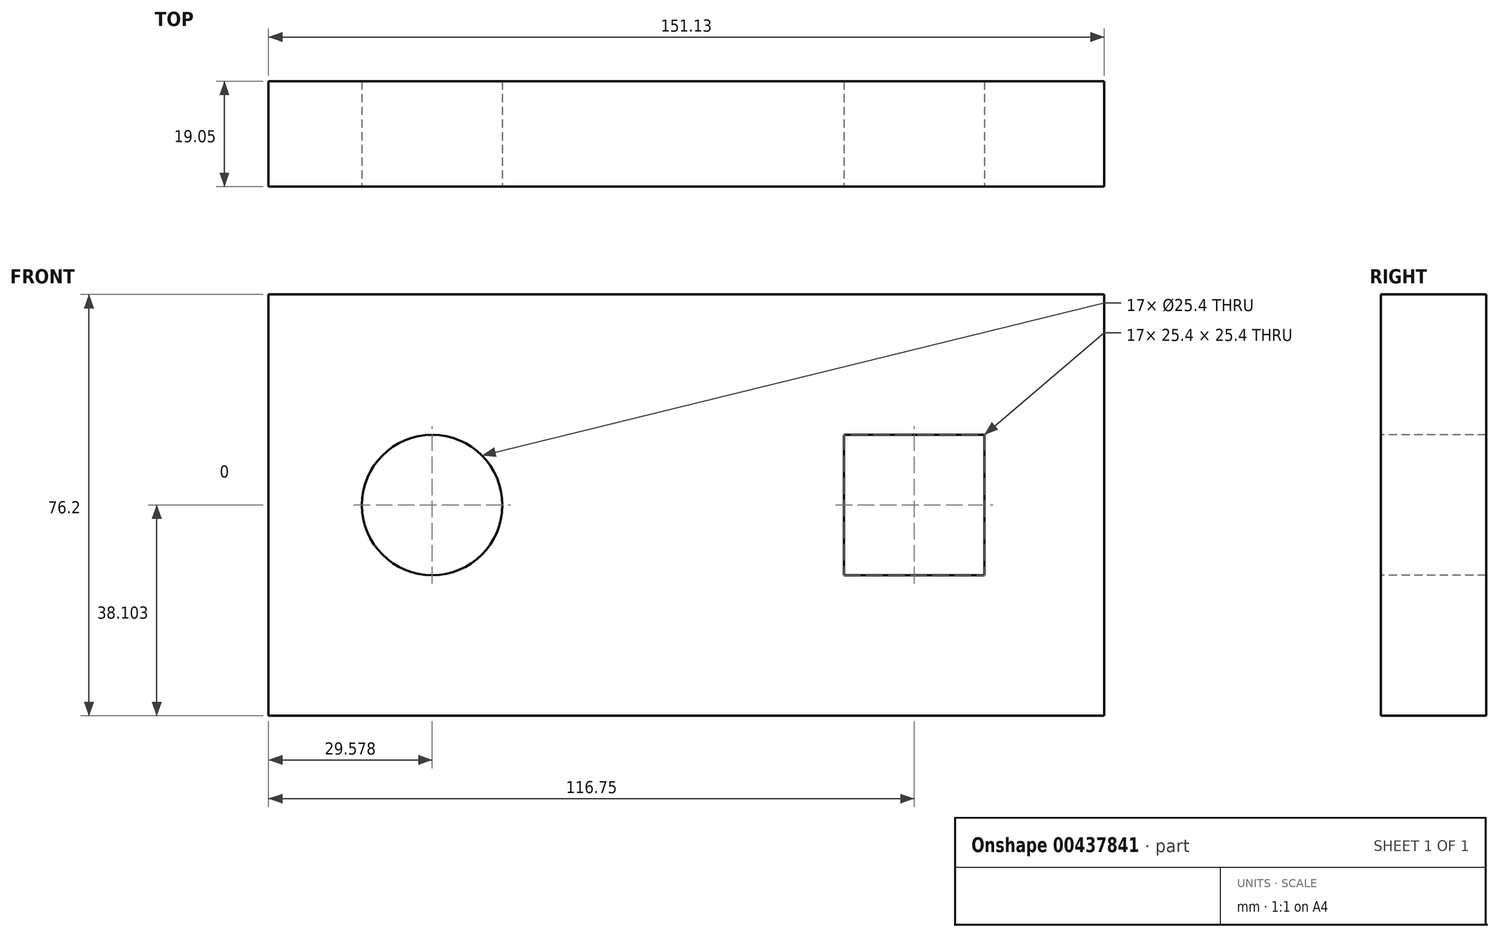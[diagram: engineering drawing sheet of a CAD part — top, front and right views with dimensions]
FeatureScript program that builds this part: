
annotation { "Feature Type Name" : "Feature", "Feature Type Description" : "" }
export const myFeature = defineFeature(function(context is Context, id is Id, definition is map)
    precondition{}
    {
        {
            var Q0;
            Q0=qCreatedBy(makeId("Front.planeOp"),FACE);
            var sketch = newSketch(context, id + "F0", { "sketchPlane" : qUnion([Q0])});
            skLineSegment(sketch, "E0.bottom", {"start": v(-75.21, 66.17) * mm, "end": v(75.92, 66.17) * mm});
            skLineSegment(sketch, "E0.top", {"start": v(-75.21, -10.03) * mm, "end": v(75.92, -10.03) * mm});
            skLineSegment(sketch, "E0.left", {"start": v(-75.21, 66.17) * mm, "end": v(-75.21, -10.03) * mm});
            skLineSegment(sketch, "E0.right", {"start": v(75.92, 66.17) * mm, "end": v(75.92, -10.03) * mm});
            skSolve(sketch);
        }
        {
            var Q0;
            Q0=makeQuery(id+"F0.imprint","IMPRINT",FACE,{"disambiguationData":[TD([[makeQuery(id+"F0.imprint","IMPRINT",EDGE,{"derivedFrom":sQuery(id+"F0.wireOp",EDGE,"E0.bottom")}),-1.0]])]});
            extrude(context, id + "F1", {"entities" : qUnion([Q0]), "depth" : 19.05 * mm});
        }
        {
            var Q0;
            Q0=makeQuery(id+"F1.opExtrude","CAP_FACE",FACE,{"disambiguationData":[OSD([sQuery(id+"F0.wireOp",EDGE,"E0.bottom"),sQuery(id+"F0.wireOp",EDGE,"E0.top"),sQuery(id+"F0.wireOp",EDGE,"E0.left"),sQuery(id+"F0.wireOp",EDGE,"E0.right")])],"isStart":false});
            var sketch = newSketch(context, id + "F2", { "sketchPlane" : qUnion([Q0])});
            skLineSegment(sketch, "E1.bottom", {"start": v(28.84, 40.77) * mm, "end": v(54.24, 40.77) * mm});
            skLineSegment(sketch, "E1.top", {"start": v(28.84, 15.37) * mm, "end": v(54.24, 15.37) * mm});
            skLineSegment(sketch, "E1.left", {"start": v(28.84, 40.77) * mm, "end": v(28.84, 15.37) * mm});
            skLineSegment(sketch, "E1.right", {"start": v(54.24, 40.77) * mm, "end": v(54.24, 15.37) * mm});
            skPoint(sketch, "E1.middle", {"position": v(41.54, 28.07) * mm});
            skPoint(sketch, "E1.middle.positionSnap0", {"position": v(75.92, 28.07) * mm});
            skPoint(sketch, "E1.centerSnap0", {"position": v(75.92, 28.07) * mm});
            skCircle(sketch, "E2", {"center": v(-45.63, 28.07) * mm, "radius": 12.7 * mm});
            skPoint(sketch, "E2.centerSnap0", {"position": v(-75.21, 28.07) * mm});
            skSolve(sketch);
        }
        {
            var Q0;
            Q0=makeQuery(id+"F2.imprint","IMPRINT",FACE,{"disambiguationData":[TD([[makeQuery(id+"F2.imprint","IMPRINT",EDGE,{"derivedFrom":sQuery(id+"F2.wireOp",EDGE,"E1.bottom")}),-1.0]])]});
            extrude(context, id + "F3", {"entities" : qUnion([Q0]), "operationType" : NewBodyOperationType.REMOVE, "oppositeDirection" : true, "depth" : 19.05 * mm});
        }
        {
            var Q0;
            Q0=makeQuery(id+"F2.imprint","IMPRINT",FACE,{"disambiguationData":[TD([[makeQuery(id+"F2.imprint","IMPRINT",EDGE,{"derivedFrom":sQuery(id+"F2.wireOp",EDGE,"E2")}),1.0]])]});
            extrude(context, id + "F4", {"entities" : qUnion([Q0]), "operationType" : NewBodyOperationType.REMOVE, "oppositeDirection" : true, "depth" : 19.05 * mm});
        }
    });
